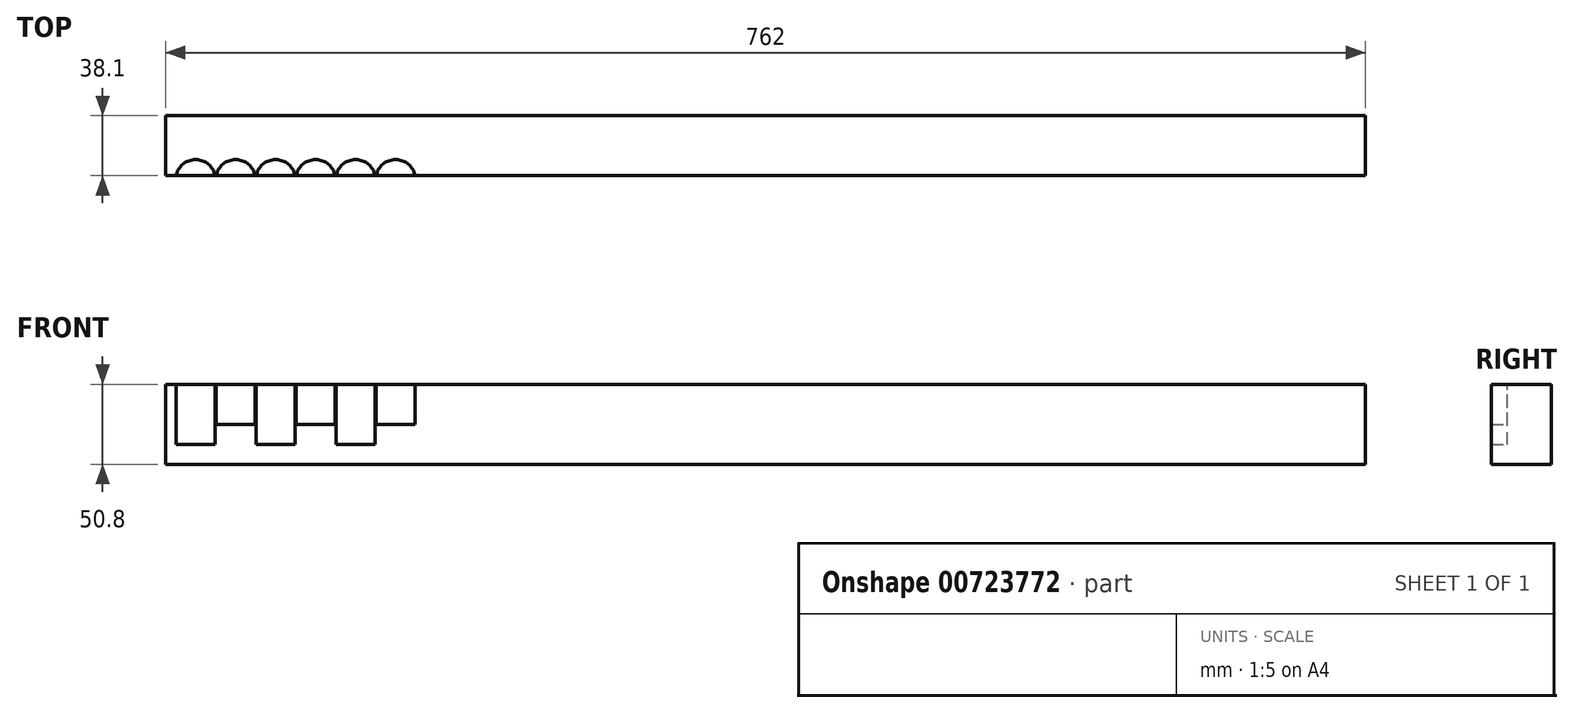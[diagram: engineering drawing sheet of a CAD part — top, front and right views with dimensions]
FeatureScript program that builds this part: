
annotation { "Feature Type Name" : "Feature", "Feature Type Description" : "" }
export const myFeature = defineFeature(function(context is Context, id is Id, definition is map)
    precondition{}
    {
        {
            var Q0;
            Q0=qCreatedBy(makeId("Right.planeOp"),FACE);
            var sketch = newSketch(context, id + "F0", { "sketchPlane" : qUnion([Q0])});
            skLineSegment(sketch, "E0.bottom", {"start": v(0, 0) * mm, "end": v(38.1, 0) * mm});
            skLineSegment(sketch, "E0.top", {"start": v(0, 50.8) * mm, "end": v(38.1, 50.8) * mm});
            skLineSegment(sketch, "E0.left", {"start": v(0, 0) * mm, "end": v(0, 50.8) * mm});
            skLineSegment(sketch, "E0.right", {"start": v(38.1, 0) * mm, "end": v(38.1, 50.8) * mm});
            skSolve(sketch);
        }
        {
            var Q0;
            Q0=makeQuery(id+"F0.imprint","IMPRINT",FACE,{"disambiguationData":[TD([[makeQuery(id+"F0.imprint","IMPRINT",EDGE,{"derivedFrom":sQuery(id+"F0.wireOp",EDGE,"E0.bottom")}),1.0]])]});
            extrude(context, id + "F1", {"entities" : qUnion([Q0]), "depth" : 762 * mm, "offsetDistance" : 25.4 * mm});
        }
        {
            var Q0;
            Q0=makeQuery(id+"F1.opExtrude","SWEPT_FACE",FACE,{"disambiguationData":[OSD([sQuery(id+"F0.wireOp",EDGE,"E0.top")])]});
            var sketch = newSketch(context, id + "F2", { "sketchPlane" : qUnion([Q0])});
            skLineSegment(sketch, "E1", {"start": v(0, 0) * mm, "end": v(0, -2.54) * mm});
            skLineSegment(sketch, "E2", {"start": v(0, -2.54) * mm, "end": v(19.05, -2.54) * mm});
            skCircle(sketch, "E3", {"center": v(19.05, -2.54) * mm, "radius": 12.7 * mm});
            skCircle(sketch, "E4.1.0.0", {"center": v(69.85, -2.54) * mm, "radius": 12.7 * mm});
            skLineSegment(sketch, "E4.1.0.1", {"start": v(50.8, -2.54) * mm, "end": v(69.85, -2.54) * mm});
            skLineSegment(sketch, "E4.1.0.2", {"start": v(50.8, 0) * mm, "end": v(50.8, -2.54) * mm});
            skCircle(sketch, "E4.2.0.0", {"center": v(120.65, -2.54) * mm, "radius": 12.7 * mm});
            skLineSegment(sketch, "E4.2.0.1", {"start": v(101.6, -2.54) * mm, "end": v(120.65, -2.54) * mm});
            skLineSegment(sketch, "E4.2.0.2", {"start": v(101.6, 0) * mm, "end": v(101.6, -2.54) * mm});
            skLineSegment(sketch, "E4.direction1", {"start": v(0, -2.54) * mm, "end": v(50.8, -2.54) * mm, "construction": true});
            skSolve(sketch);
        }
        {
            var Q0;
            Q0 = qSketchRegion(id + "F2", true);
            extrude(context, id + "F3", {"entities" : qUnion([Q0]), "operationType" : NewBodyOperationType.REMOVE, "oppositeDirection" : true, "depth" : 38.1 * mm, "offsetDistance" : 25.4 * mm});
        }
        {
            var Q0;
            Q0=makeQuery(id+"F1.opExtrude","SWEPT_FACE",FACE,{"disambiguationData":[OSD([sQuery(id+"F0.wireOp",EDGE,"E0.top")])]});
            var sketch = newSketch(context, id + "F4", { "sketchPlane" : qUnion([Q0])});
            skLineSegment(sketch, "E5", {"start": v(0, 0) * mm, "end": v(0, -2.54) * mm});
            skLineSegment(sketch, "E6", {"start": v(0, -2.54) * mm, "end": v(44.45, -2.54) * mm});
            skCircle(sketch, "E7", {"center": v(44.45, -2.54) * mm, "radius": 12.7 * mm});
            skLineSegment(sketch, "E8.1.0.0", {"start": v(50.8, -2.54) * mm, "end": v(95.25, -2.54) * mm});
            skLineSegment(sketch, "E8.1.0.1", {"start": v(50.8, 0) * mm, "end": v(50.8, -2.54) * mm});
            skCircle(sketch, "E8.1.0.2", {"center": v(95.25, -2.54) * mm, "radius": 12.7 * mm});
            skLineSegment(sketch, "E8.2.0.0", {"start": v(101.6, -2.54) * mm, "end": v(146.05, -2.54) * mm});
            skLineSegment(sketch, "E8.2.0.1", {"start": v(101.6, 0) * mm, "end": v(101.6, -2.54) * mm});
            skCircle(sketch, "E8.2.0.2", {"center": v(146.05, -2.54) * mm, "radius": 12.7 * mm});
            skLineSegment(sketch, "E8.direction1", {"start": v(0, -2.54) * mm, "end": v(50.8, -2.54) * mm, "construction": true});
            skSolve(sketch);
        }
        {
            var Q0;
            Q0 = qSketchRegion(id + "F4", true);
            extrude(context, id + "F5", {"entities" : qUnion([Q0]), "operationType" : NewBodyOperationType.REMOVE, "oppositeDirection" : true, "depth" : 25.4 * mm, "offsetDistance" : 25.4 * mm});
        }
    });
